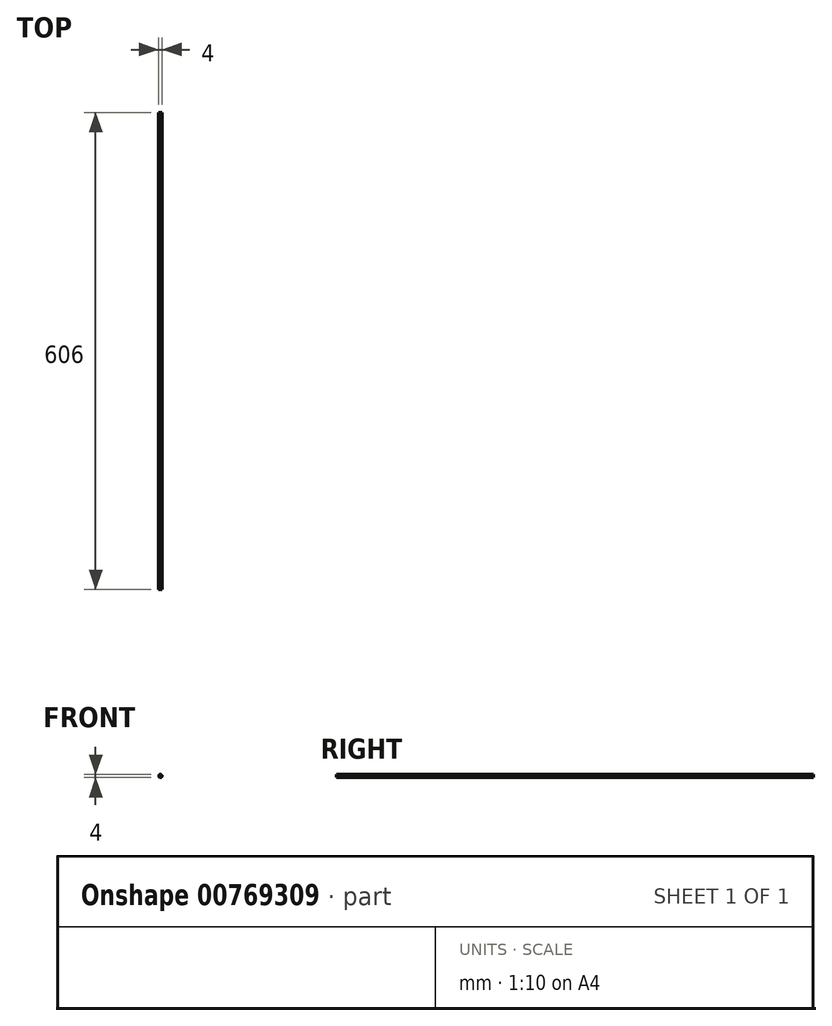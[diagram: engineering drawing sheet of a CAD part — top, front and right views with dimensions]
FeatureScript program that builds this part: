
annotation { "Feature Type Name" : "Feature", "Feature Type Description" : "" }
export const myFeature = defineFeature(function(context is Context, id is Id, definition is map)
    precondition{}
    {
        {
            var Q0;
            Q0=qCreatedBy(makeId("Front.planeOp"),FACE);
            var sketch = newSketch(context, id + "F0", { "sketchPlane" : qUnion([Q0])});
            skCircle(sketch, "E0", {"center": v(0, 0) * mm, "radius": 2 * mm});
            skSolve(sketch);
        }
        {
            var Q0;
            Q0=makeQuery(id+"F0.imprint","IMPRINT",FACE,{"disambiguationData":[TD([[makeQuery(id+"F0.imprint","IMPRINT",EDGE,{"derivedFrom":sQuery(id+"F0.wireOp",EDGE,"E0")}),1.0]])]});
            extrude(context, id + "F1", {"entities" : qUnion([Q0]), "depth" : 606 * mm, "offsetDistance" : 25 * mm});
        }
    });
